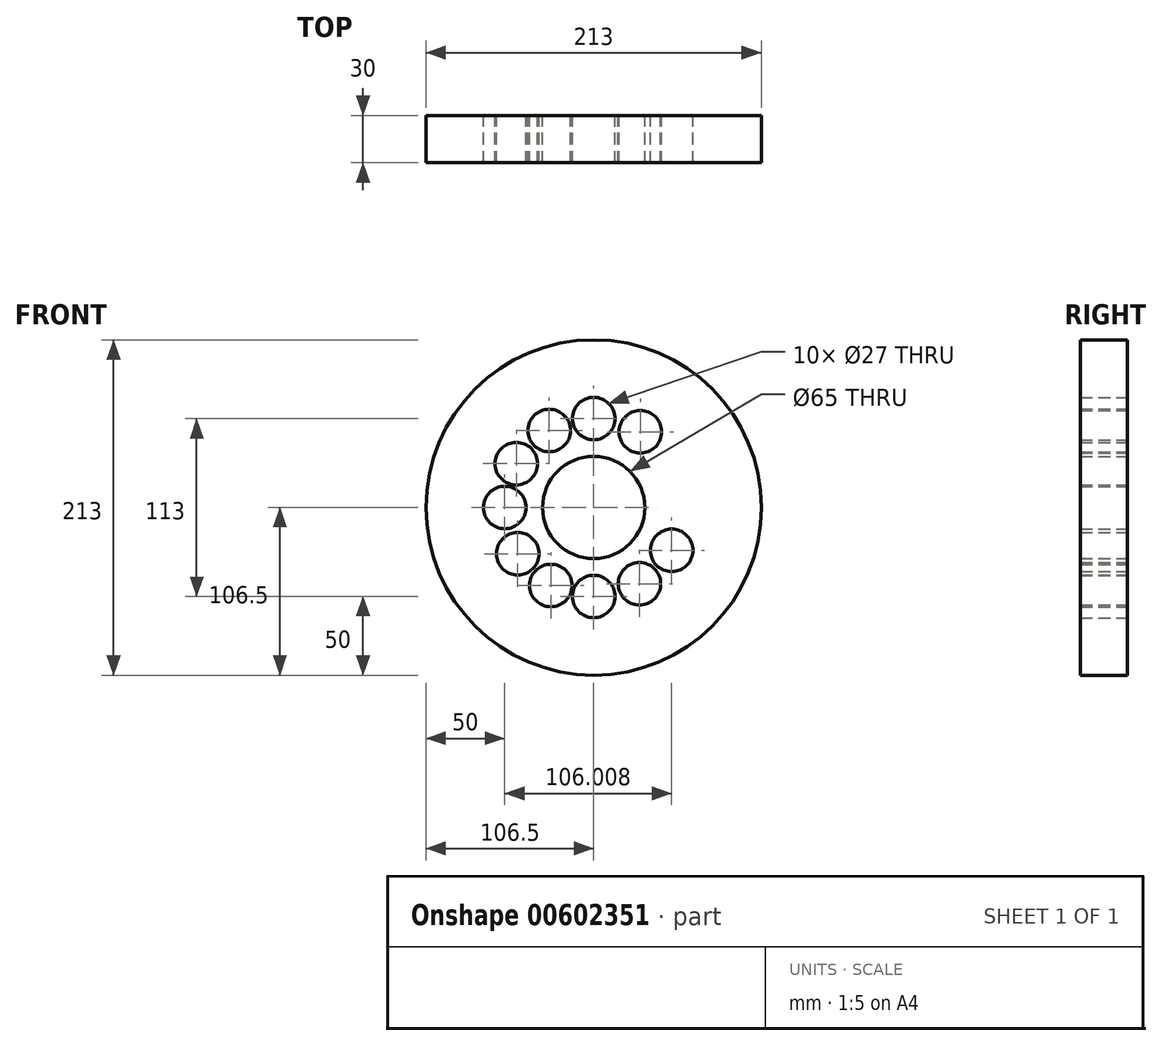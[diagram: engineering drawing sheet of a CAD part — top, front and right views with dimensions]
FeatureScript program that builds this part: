
annotation { "Feature Type Name" : "Feature", "Feature Type Description" : "" }
export const myFeature = defineFeature(function(context is Context, id is Id, definition is map)
    precondition{}
    {
        {
            var Q0;
            Q0=qCreatedBy(makeId("Front.planeOp"),FACE);
            var sketch = newSketch(context, id + "F0", { "sketchPlane" : qUnion([Q0])});
            skCircle(sketch, "E0", {"center": v(0, 0) * mm, "radius": 32.5 * mm});
            skCircle(sketch, "E1", {"center": v(0, 0) * mm, "radius": 37.5 * mm});
            skCircle(sketch, "E2", {"center": v(0, 0) * mm, "radius": 75 * mm});
            skCircle(sketch, "E3", {"center": v(0, 56.5) * mm, "radius": 13.5 * mm});
            skCircle(sketch, "E4", {"center": v(-56.5, 0) * mm, "radius": 13.5 * mm});
            skCircle(sketch, "E5", {"center": v(-49.15, 27.87) * mm, "radius": 13.5 * mm});
            skCircle(sketch, "E6", {"center": v(-28.26, 48.92) * mm, "radius": 13.5 * mm});
            skCircle(sketch, "E7", {"center": v(29.63, 48.1) * mm, "radius": 13.5 * mm});
            skCircle(sketch, "E8", {"center": v(0, -56.5) * mm, "radius": 13.5 * mm});
            skCircle(sketch, "E9", {"center": v(-48.26, -29.38) * mm, "radius": 13.5 * mm});
            skCircle(sketch, "E10", {"center": v(-27.22, -49.5) * mm, "radius": 13.5 * mm});
            skCircle(sketch, "E11", {"center": v(29.07, -48.45) * mm, "radius": 13.5 * mm});
            skCircle(sketch, "E12", {"center": v(49.5, -27.22) * mm, "radius": 13.5 * mm});
            skCircle(sketch, "E13", {"center": v(0, 0) * mm, "radius": 106.5 * mm});
            skSolve(sketch);
        }
        {
            var Q0;
            Q0=makeQuery(id+"F0.imprint","IMPRINT",FACE,{"disambiguationData":[TD([[makeQuery(id+"F0.imprint","IMPRINT",EDGE,{"derivedFrom":sQuery(id+"F0.wireOp",EDGE,"E1")}),-1.0]])]});
            var Q1;
            Q1=makeQuery(id+"F0.imprint","IMPRINT",FACE,{"disambiguationData":[TD([[makeQuery(id+"F0.imprint","IMPRINT",EDGE,{"derivedFrom":sQuery(id+"F0.wireOp",EDGE,"E2")}),-1.0]])]});
            var Q2;
            Q2=makeQuery(id+"F0.imprint","IMPRINT",FACE,{"disambiguationData":[TD([[makeQuery(id+"F0.imprint","IMPRINT",EDGE,{"derivedFrom":sQuery(id+"F0.wireOp",EDGE,"E0")}),-1.0]])]});
            extrude(context, id + "F1", {"entities" : qUnion([Q0, Q1, Q2]), "depth" : 30 * mm, "offsetDistance" : 25 * mm});
        }
    });
